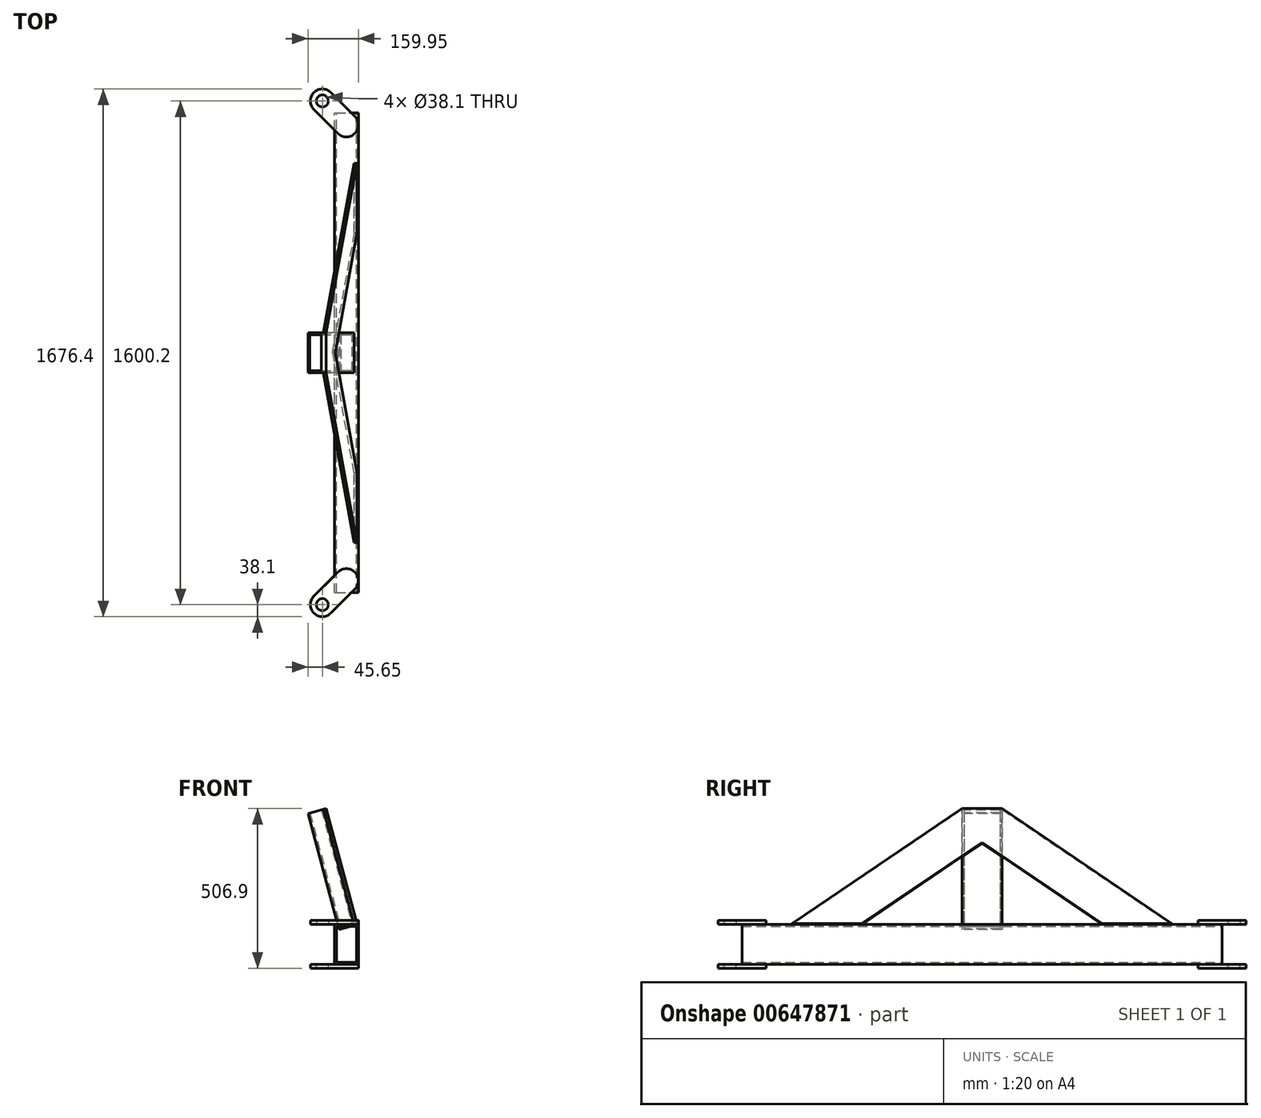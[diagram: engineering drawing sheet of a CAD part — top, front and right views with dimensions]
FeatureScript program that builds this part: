
annotation { "Feature Type Name" : "Feature", "Feature Type Description" : "" }
export const myFeature = defineFeature(function(context is Context, id is Id, definition is map)
    precondition{}
    {
        {
            var Q0;
            Q0=qCreatedBy(makeId("Front.planeOp"),FACE);
            var sketch = newSketch(context, id + "F0", { "sketchPlane" : qUnion([Q0])});
            skLineSegment(sketch, "E0.bottom", {"start": v(0, 63.5) * mm, "end": v(76.2, 63.5) * mm});
            skLineSegment(sketch, "E0.top", {"start": v(0, -63.5) * mm, "end": v(76.2, -63.5) * mm});
            skLineSegment(sketch, "E0.left", {"start": v(0, 63.5) * mm, "end": v(0, -63.5) * mm});
            skLineSegment(sketch, "E0.right", {"start": v(76.2, 63.5) * mm, "end": v(76.2, -63.5) * mm});
            skLineSegment(sketch, "E1.bottom", {"start": v(6.35, 57.15) * mm, "end": v(69.85, 57.15) * mm});
            skLineSegment(sketch, "E1.top", {"start": v(6.35, -57.15) * mm, "end": v(69.85, -57.15) * mm});
            skLineSegment(sketch, "E1.left", {"start": v(6.35, 57.15) * mm, "end": v(6.35, -57.15) * mm});
            skLineSegment(sketch, "E1.right", {"start": v(69.85, 57.15) * mm, "end": v(69.85, -57.15) * mm});
            skSolve(sketch);
        }
        {
            var Q0;
            Q0 = qSketchRegion(id + "F0", true);
            extrude(context, id + "F1", {"entities" : qUnion([Q0]), "endBound" : BoundingType.SYMMETRIC, "depth" : 1524 * mm, "offsetDistance" : 25.4 * mm});
        }
        {
            var Q0;
            Q0=makeQuery(id+"F1.opExtrude","SWEPT_FACE",FACE,{"disambiguationData":[OSD([sQuery(id+"F0.wireOp",EDGE,"E0.bottom")])]});
            var sketch = newSketch(context, id + "F2", { "sketchPlane" : qUnion([Q0])});
            skLineSegment(sketch, "E2", {"start": v(-65.04, 773.16) * mm, "end": v(11.16, 696.96) * mm});
            skArc(sketch, "E3", {"start": v(-65.04, 773.16) * mm, "mid": v(-65.04, 827.04) * mm, "end": v(-11.16, 827.04) * mm});
            skLineSegment(sketch, "E4", {"start": v(65.04, 750.84) * mm, "end": v(-11.16, 827.04) * mm});
            skArc(sketch, "E5", {"start": v(65.04, 750.84) * mm, "mid": v(65.04, 696.96) * mm, "end": v(11.16, 696.96) * mm});
            skCircle(sketch, "E6", {"center": v(-38.1, 800.1) * mm, "radius": 19.05 * mm});
            skSolve(sketch);
        }
        {
            var Q0;
            Q0 = qSketchRegion(id + "F2", true);
            extrude(context, id + "F3", {"entities" : qUnion([Q0]), "operationType" : NewBodyOperationType.ADD, "depth" : 12.7 * mm, "offsetDistance" : 25.4 * mm});
        }
        {
            var Q0;
            Q0=makeQuery(id+"F1.opExtrude","SWEPT_BODY",BODY,{"disambiguationData":[OSD([sQuery(id+"F0.wireOp",EDGE,"E0.bottom"),sQuery(id+"F0.wireOp",EDGE,"E0.top"),sQuery(id+"F0.wireOp",EDGE,"E0.left"),sQuery(id+"F0.wireOp",EDGE,"E0.right"),sQuery(id+"F0.wireOp",EDGE,"E1.bottom"),sQuery(id+"F0.wireOp",EDGE,"E1.top"),sQuery(id+"F0.wireOp",EDGE,"E1.left"),sQuery(id+"F0.wireOp",EDGE,"E1.right")])]});
            var Q1;
            Q1=qCreatedBy(makeId("Top.planeOp"),FACE);
            mirror(context, id + "F4", {"operationType" : NewBodyOperationType.ADD, "entities" : qUnion([Q0]), "mirrorPlane" : qUnion([Q1])});
        }
        {
            var Q0;
            Q0=makeQuery(id+"F1.opExtrude","SWEPT_FACE",FACE,{"disambiguationData":[OSD([sQuery(id+"F0.wireOp",EDGE,"E0.right")])]});
            cPlane(context, id + "F5", {"entities" : qUnion([Q0]), "cplaneType" : CPlaneType.OFFSET, "offset" : 38.1 * mm, "oppositeDirection" : true, "width" : 152.4 * mm, "height" : 152.4 * mm});
        }
        {
            var Q0;
            Q0=qCreatedBy(id+"F5.planeOp",FACE);
            var sketch = newSketch(context, id + "F6", { "sketchPlane" : qUnion([Q0])});
            skLineSegment(sketch, "E7", {"start": v(-254, 63.5) * mm, "end": v(-129.42, 370.09) * mm});
            skLineSegment(sketch, "E8", {"start": v(254, 63.5) * mm, "end": v(129.42, 370.09) * mm});
            skArc(sketch, "E9", {"start": v(-129.42, 370.09) * mm, "mid": v(0, 457.2) * mm, "end": v(129.42, 370.09) * mm});
            skSolve(sketch);
        }
        {
            var Q0;
            {var subQ0=sQuery(id+"F0.wireOp",EDGE,"E0.bottom");var subQ1=makeQuery(id+"F1.opExtrude","CAP_EDGE",EDGE,{"disambiguationData":[OSD([subQ0])],"isStart":false});Q0=makeQuery(id+"F2.imprint","IMPRINT",FACE,{"disambiguationData":[TD([[makeQuery(id+"F2.imprint","IMPRINT",EDGE,{"derivedFrom":subQ1}),1.0]])]});}
            var sketch = newSketch(context, id + "F7", { "sketchPlane" : qUnion([Q0])});
            skCircle(sketch, "E10", {"center": v(38.1, -254) * mm, "radius": 19.05 * mm});
            skSolve(sketch);
        }
        {
            var Q0;
            {var subQ0=sQuery(id+"F0.wireOp",EDGE,"E0.bottom");var subQ1=sQuery(id+"F0.wireOp",EDGE,"E0.right");Q0=makeQuery(id+"F3.boolean.opBoolean","SPLIT",EDGE,{"disambiguationData":[TD([makeQuery(id+"F1.opExtrude","CAP_FACE",FACE,{"disambiguationData":[OSD([subQ0,sQuery(id+"F0.wireOp",EDGE,"E0.top"),sQuery(id+"F0.wireOp",EDGE,"E0.left"),subQ1,sQuery(id+"F0.wireOp",EDGE,"E1.bottom"),sQuery(id+"F0.wireOp",EDGE,"E1.top"),sQuery(id+"F0.wireOp",EDGE,"E1.left"),sQuery(id+"F0.wireOp",EDGE,"E1.right")])],"isStart":false})])],"derivedFrom":makeQuery(id+"F1.opExtrude","SWEPT_EDGE",EDGE,{"disambiguationData":[OSD([subQ0,subQ1])]})});}
            cPlane(context, id + "F8", {"entities" : qUnion([Q0]), "cplaneType" : CPlaneType.LINE_ANGLE, "offset" : 25.4 * mm, "angle" : 15 * degree, "oppositeDirection" : true, "width" : 152.4 * mm, "height" : 152.4 * mm});
        }
        {
            var Q0;
            Q0=qCreatedBy(id+"F8.planeOp",FACE);
            var sketch = newSketch(context, id + "F9", { "sketchPlane" : qUnion([Q0])});
            skLineSegment(sketch, "E11.bottom", {"start": v(77.34, 63.5) * mm, "end": v(26.54, 63.5) * mm});
            skLineSegment(sketch, "E11.top", {"start": v(77.34, -63.5) * mm, "end": v(26.54, -63.5) * mm});
            skLineSegment(sketch, "E11.left", {"start": v(77.34, 63.5) * mm, "end": v(77.34, -63.5) * mm});
            skLineSegment(sketch, "E11.right", {"start": v(26.54, 63.5) * mm, "end": v(26.54, -63.5) * mm});
            skLineSegment(sketch, "E12.0", {"start": v(70.99, 57.15) * mm, "end": v(70.99, -57.15) * mm});
            skLineSegment(sketch, "E12.1", {"start": v(70.99, 57.15) * mm, "end": v(32.89, 57.15) * mm});
            skLineSegment(sketch, "E12.2", {"start": v(32.89, 57.15) * mm, "end": v(32.89, -57.15) * mm});
            skLineSegment(sketch, "E12.3", {"start": v(70.99, -57.15) * mm, "end": v(32.89, -57.15) * mm});
            skSolve(sketch);
        }
        {
            var Q0;
            Q0 = qSketchRegion(id + "F9", true);
            extrude(context, id + "F10", {"entities" : qUnion([Q0]), "operationType" : NewBodyOperationType.ADD, "depth" : 381 * mm, "offsetDistance" : 25.4 * mm});
        }
        {
            var Q0;
            Q0=makeQuery(id+"F10.opExtrude","SWEPT_FACE",FACE,{"disambiguationData":[OSD([sQuery(id+"F9.wireOp",EDGE,"E11.left")])]});
            var sketch = newSketch(context, id + "F11", { "sketchPlane" : qUnion([Q0])});
            skLineSegment(sketch, "E13", {"start": v(-63.5, 422.61) * mm, "end": v(-602.76, 45.02) * mm});
            skLineSegment(sketch, "E14", {"start": v(-602.76, 45.02) * mm, "end": v(-381.35, 45.02) * mm});
            skLineSegment(sketch, "E15", {"start": v(-381.35, 45.02) * mm, "end": v(0, 312.04) * mm});
            skLineSegment(sketch, "E16", {"start": v(0, 312.04) * mm, "end": v(0, 422.61) * mm});
            skLineSegment(sketch, "E17", {"start": v(0, 422.61) * mm, "end": v(-63.5, 422.61) * mm});
            skSolve(sketch);
        }
        {
            var Q0;
            Q0 = qSketchRegion(id + "F11", true);
            extrude(context, id + "F12", {"entities" : qUnion([Q0]), "operationType" : NewBodyOperationType.ADD, "depth" : 9.52 * mm, "offsetDistance" : 25.4 * mm, "hasSecondDirection" : true, "secondDirectionOppositeDirection" : true, "secondDirectionDepth" : 0.25 * mm});
        }
        {
            var Q0;
            Q0=makeQuery(id+"F1.opExtrude","SWEPT_BODY",BODY,{"disambiguationData":[OSD([sQuery(id+"F0.wireOp",EDGE,"E0.bottom"),sQuery(id+"F0.wireOp",EDGE,"E0.top"),sQuery(id+"F0.wireOp",EDGE,"E0.left"),sQuery(id+"F0.wireOp",EDGE,"E0.right"),sQuery(id+"F0.wireOp",EDGE,"E1.bottom"),sQuery(id+"F0.wireOp",EDGE,"E1.top"),sQuery(id+"F0.wireOp",EDGE,"E1.left"),sQuery(id+"F0.wireOp",EDGE,"E1.right")])]});
            var Q1;
            Q1=makeQuery(id+"F12.opExtrude","SWEPT_FACE",FACE,{"disambiguationData":[OSD([sQuery(id+"F11.wireOp",EDGE,"E16")])]});
            mirror(context, id + "F13", {"operationType" : NewBodyOperationType.ADD, "entities" : qUnion([Q0]), "mirrorPlane" : qUnion([Q1])});
        }
    });
